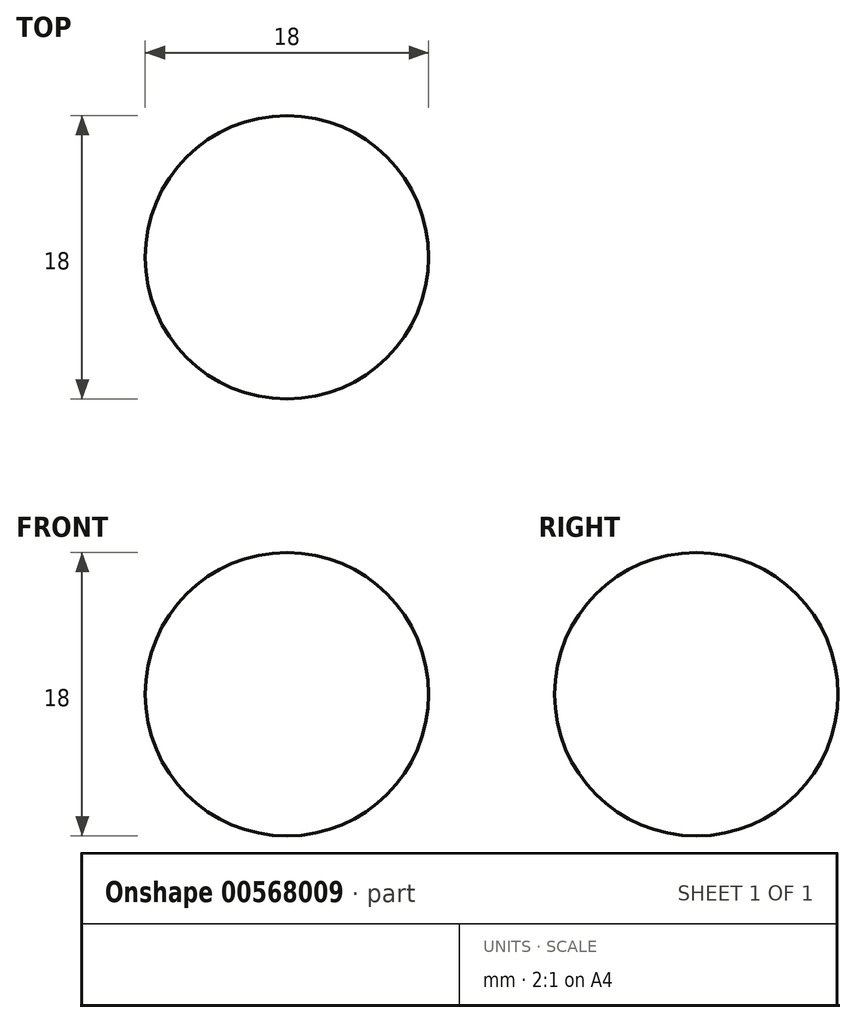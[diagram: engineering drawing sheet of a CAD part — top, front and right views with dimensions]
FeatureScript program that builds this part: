
annotation { "Feature Type Name" : "Feature", "Feature Type Description" : "" }
export const myFeature = defineFeature(function(context is Context, id is Id, definition is map)
    precondition{}
    {
        {
            var Q0;
            Q0=qCreatedBy(makeId("Top.planeOp"),FACE);
            var sketch = newSketch(context, id + "F0", { "sketchPlane" : qUnion([Q0])});
            skCircle(sketch, "E0", {"center": v(0, 0) * mm, "radius": 9.5 * mm});
            skSolve(sketch);
        }
        {
            var Q0;
            Q0=qCreatedBy(makeId("Top.planeOp"),FACE);
            var sketch = newSketch(context, id + "F1", { "sketchPlane" : qUnion([Q0])});
            skLineSegment(sketch, "E1", {"start": v(0, 0) * mm, "end": v(0, 9) * mm});
            skArc(sketch, "E2", {"start": v(0, 9) * mm, "mid": v(9, 0) * mm, "end": v(0, -9) * mm});
            skSolve(sketch);
        }
        {
            var Q0;
            Q0=sQuery(id+"F1.wireOp",EDGE,"E2");
            var Q1;
            Q1=sQuery(id+"F1.wireOp",EDGE,"E1");
            revolve(context, id + "F2", {"bodyType" : ToolBodyType.SURFACE, "surfaceEntities" : qUnion([Q0]), "axis" : qUnion([Q1]), "revolveType" : RevolveType.FULL});
        }
    });
